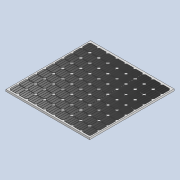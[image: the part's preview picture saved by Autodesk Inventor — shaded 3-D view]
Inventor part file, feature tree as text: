
AUTODESK INVENTOR PART (.ipt)
format: ipt  version: 2021 (Build 250183000, 183)  size: 2,149,888 bytes
history: native  units: in
note: dims shown in document units (in); Inventor stores cm internally (conversion verified against a paired STEP export)
features: extrude x3, sketch x3, plane x2, split x2, projected_geometry x2, direct_edit x1, mirror x1, other x1
ambient origin geometry x8: Origin, YZ Plane, XZ Plane, XY Plane, X Axis, Y Axis, Z Axis, Center Point
bodies: Solid1 (feature_tree)
feature tree (15):
  extrude  "Extrusion1"  Depth=62.5984in
  extrude  "Extrusion2"  Depth=6.2992in
  direct_edit  "Direct Edit1"
  plane  "Work Plane2"
  split  "Split2"
  mirror  "Mirror2"
  plane  "Work Plane3"
  split  "Split3"
  extrude  "Extrusion3"  Depth=0.0164in
  sketch  "Sketch1"  dims[d0=62.5984in d1=41.4567in]
  sketch  "Sketch2"  dims[d2=1.5748in d3=0.0in d5=6.2992in]
  projected_geometry  "Projected Loop1"
  sketch  "Sketch3"  dims[d6=6.2992in d7=0.7874in d8=0.7874in d9=0.7874in d10=0.7874in d11=0.7874in d12=0.7874in d13=0.7874in d14=0.7874in d15=1.1811in d16=0.1969in d17=0.1969in d18=0.1969in d19=2.3622in d21=6.6929in d22=3.5433in d24=6.6929in d27=0.1969in d28=0.0in d29=0.0164in d30=0.3937in d31=0.3937in d33=0.0093in d34=0.0in d35=0.0197in d36=0.0in]
  projected_geometry  "Projected Loop2"
  other  "Scale1"
